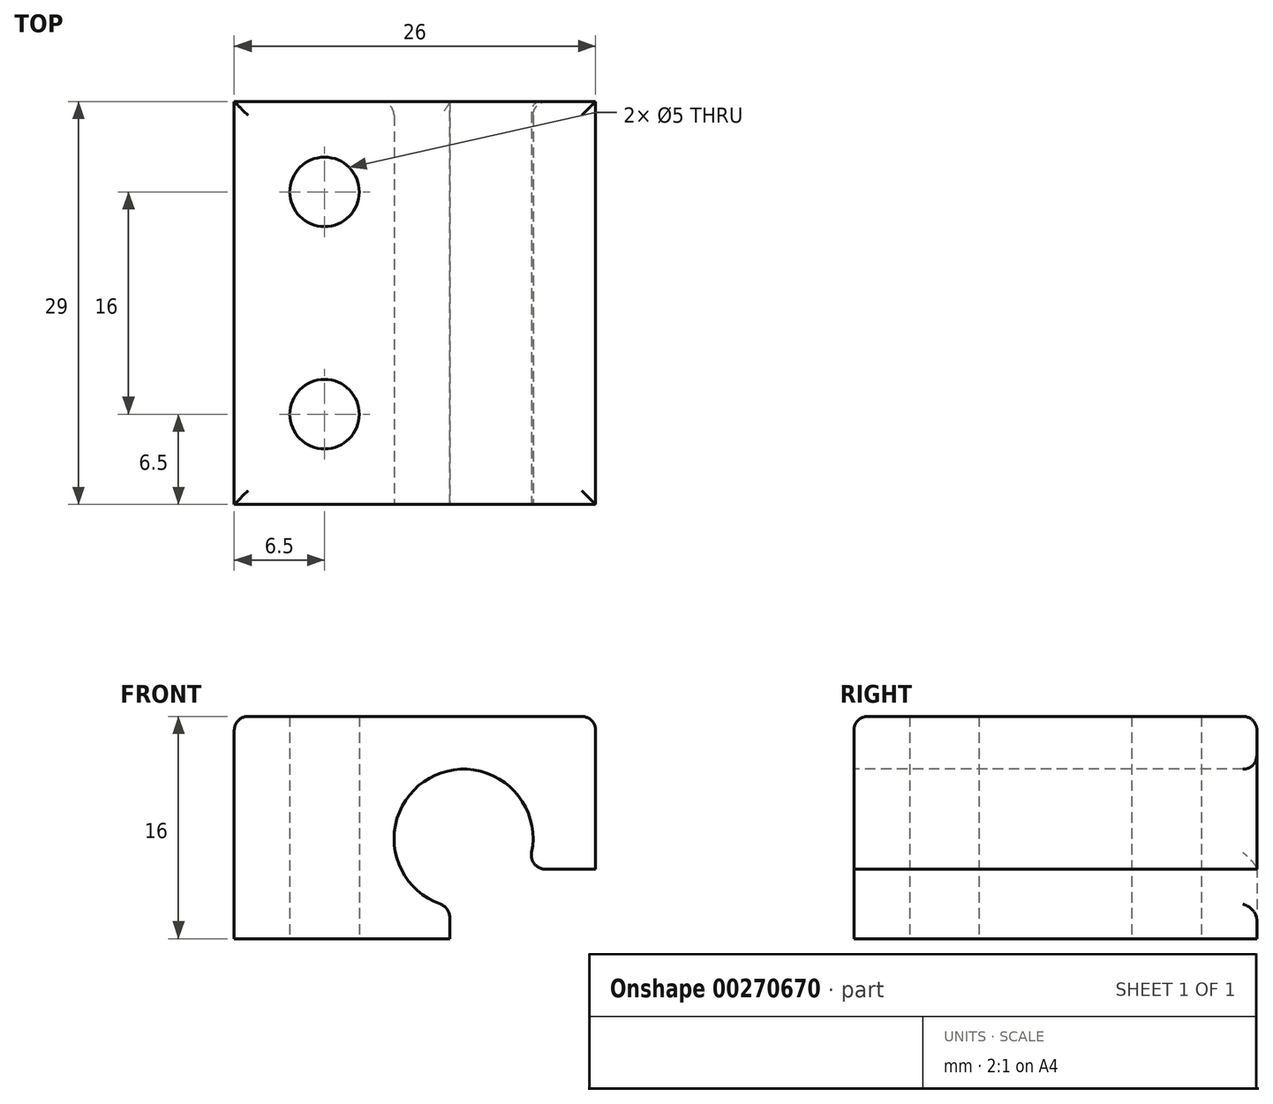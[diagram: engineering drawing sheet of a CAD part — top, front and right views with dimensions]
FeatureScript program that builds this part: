
annotation { "Feature Type Name" : "Feature", "Feature Type Description" : "" }
export const myFeature = defineFeature(function(context is Context, id is Id, definition is map)
    precondition{}
    {
        {
            var Q0;
            Q0=qCreatedBy(makeId("Top.planeOp"),FACE);
            var sketch = newSketch(context, id + "F0", { "sketchPlane" : qUnion([Q0])});
            skLineSegment(sketch, "E0.bottom", {"start": v(13, -14.5) * mm, "end": v(-13, -14.5) * mm});
            skLineSegment(sketch, "E0.top", {"start": v(13, 14.5) * mm, "end": v(-13, 14.5) * mm});
            skLineSegment(sketch, "E0.left", {"start": v(13, -14.5) * mm, "end": v(13, 14.5) * mm});
            skLineSegment(sketch, "E0.right", {"start": v(-13, -14.5) * mm, "end": v(-13, 14.5) * mm});
            skPoint(sketch, "E0.middle", {"position": v(0, 0) * mm});
            skLineSegment(sketch, "E1", {"start": v(-6.5, 14.5) * mm, "end": v(-6.5, -14.5) * mm, "construction": true});
            skCircle(sketch, "E2", {"center": v(-6.5, 8) * mm, "radius": 2.5 * mm});
            skCircle(sketch, "E3.MirrorC", {"center": v(-6.5, -8) * mm, "radius": 2.5 * mm});
            skSolve(sketch);
        }
        {
            var Q0;
            Q0 = qSketchRegion(id + "F0", true);
            extrude(context, id + "F1", {"entities" : qUnion([Q0]), "depth" : 16 * mm});
        }
        {
            var Q0;
            Q0=makeQuery(id+"F1.opExtrude","SWEPT_FACE",FACE,{"disambiguationData":[OSD([sQuery(id+"F0.wireOp",EDGE,"E0.bottom")])]});
            var sketch = newSketch(context, id + "F2", { "sketchPlane" : qUnion([Q0])});
            skCircle(sketch, "E4", {"center": v(3.5, 7.2) * mm, "radius": 5 * mm});
            skSolve(sketch);
        }
        {
            var Q0;
            Q0 = qSketchRegion(id + "F2", true);
            extrude(context, id + "F3", {"entities" : qUnion([Q0]), "operationType" : NewBodyOperationType.REMOVE, "oppositeDirection" : true, "depth" : 60 * mm});
        }
        {
            var Q0;
            Q0=makeQuery(id+"F1.opExtrude","SWEPT_FACE",FACE,{"disambiguationData":[OSD([sQuery(id+"F0.wireOp",EDGE,"E0.bottom")])]});
            var sketch = newSketch(context, id + "F4", { "sketchPlane" : qUnion([Q0])});
            skLineSegment(sketch, "E5.bottom", {"start": v(2.5, 0) * mm, "end": v(13, 0) * mm});
            skLineSegment(sketch, "E5.top", {"start": v(2.5, 5) * mm, "end": v(13, 5) * mm});
            skLineSegment(sketch, "E5.left", {"start": v(2.5, 0) * mm, "end": v(2.5, 5) * mm});
            skLineSegment(sketch, "E5.right", {"start": v(13, 0) * mm, "end": v(13, 5) * mm});
            skSolve(sketch);
        }
        {
            var Q0;
            Q0 = qSketchRegion(id + "F4", true);
            extrude(context, id + "F5", {"entities" : qUnion([Q0]), "operationType" : NewBodyOperationType.REMOVE, "oppositeDirection" : true, "depth" : 60 * mm});
        }
        {
            var Q0;
            Q0=makeQuery(id+"F1.opExtrude","CAP_EDGE",EDGE,{"disambiguationData":[OSD([sQuery(id+"F0.wireOp",EDGE,"E0.bottom")])],"isStart":false});
            var Q1;
            Q1=makeQuery(id+"F1.opExtrude","CAP_EDGE",EDGE,{"disambiguationData":[OSD([sQuery(id+"F0.wireOp",EDGE,"E0.right")])],"isStart":false});
            var Q2;
            Q2=makeQuery(id+"F1.opExtrude","CAP_EDGE",EDGE,{"disambiguationData":[OSD([sQuery(id+"F0.wireOp",EDGE,"E0.left")])],"isStart":false});
            var Q3;
            Q3=makeQuery(id+"F1.opExtrude","CAP_EDGE",EDGE,{"disambiguationData":[OSD([sQuery(id+"F0.wireOp",EDGE,"E0.top")])],"isStart":false});
            var Q4;
            Q4=makeQuery(id+"F5.boolean.opBoolean","INTERSECT",EDGE,{"derivedFrom":[makeQuery(id+"F3.boolean.opBoolean","COPY",FACE,{"derivedFrom":makeQuery(id+"F3.opExtrude","SWEPT_FACE",FACE,{"disambiguationData":[OSD([sQuery(id+"F2.wireOp",EDGE,"E4")])]})}),makeQuery(id+"F5.opExtrude","SWEPT_FACE",FACE,{"disambiguationData":[OSD([sQuery(id+"F4.wireOp",EDGE,"E5.top")])]})]});
            var Q5;
            Q5=makeQuery(id+"F5.boolean.opBoolean","INTERSECT",EDGE,{"derivedFrom":[makeQuery(id+"F3.boolean.opBoolean","COPY",FACE,{"derivedFrom":makeQuery(id+"F3.opExtrude","SWEPT_FACE",FACE,{"disambiguationData":[OSD([sQuery(id+"F2.wireOp",EDGE,"E4")])]})}),makeQuery(id+"F5.opExtrude","SWEPT_FACE",FACE,{"disambiguationData":[OSD([sQuery(id+"F4.wireOp",EDGE,"E5.left")])]})]});
            var Q6;
            Q6=makeQuery(id+"F3.boolean.opBoolean","COPY",EDGE,{"derivedFrom":makeQuery(id+"F3.opExtrude","CAP_EDGE",EDGE,{"disambiguationData":[OSD([sQuery(id+"F2.wireOp",EDGE,"E4")])],"isStart":true})});
            var Q7;
            Q7=makeQuery(id+"F3.boolean.opBoolean","INTERSECT",EDGE,{"derivedFrom":[makeQuery(id+"F1.opExtrude","SWEPT_FACE",FACE,{"disambiguationData":[OSD([sQuery(id+"F0.wireOp",EDGE,"E0.top")])]}),makeQuery(id+"F3.opExtrude","SWEPT_FACE",FACE,{"disambiguationData":[OSD([sQuery(id+"F2.wireOp",EDGE,"E4")])]})]});
            fillet(context, id + "F6", {"entities" : qUnion([Q0, Q1, Q2, Q3, Q4, Q5, Q6, Q7]), "radius" : 1 * mm, "tangentPropagation" : true, "allowEdgeOverflow" : false});
        }
    });
